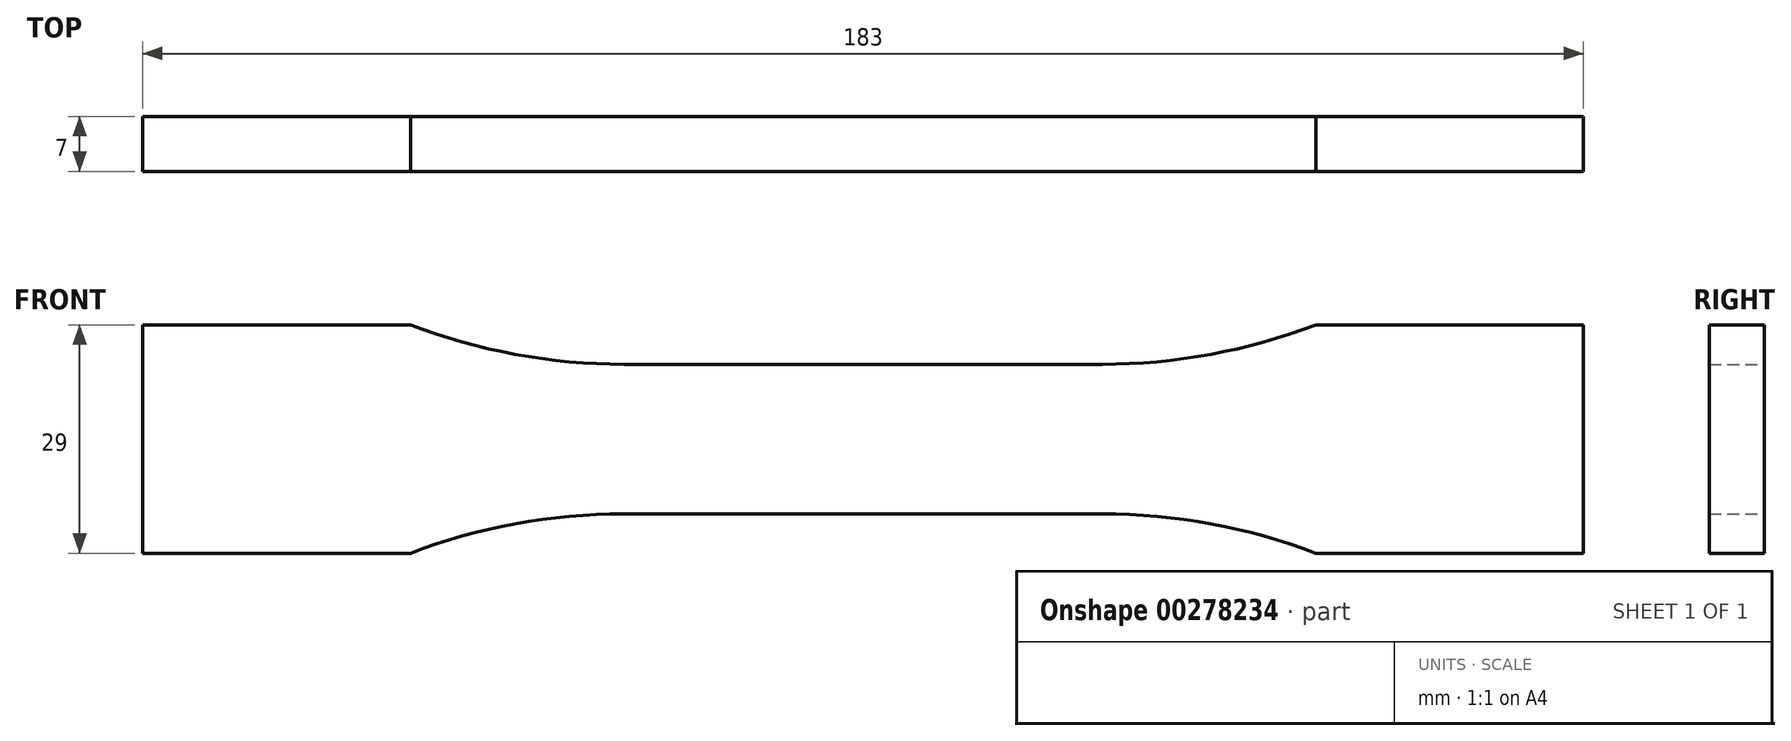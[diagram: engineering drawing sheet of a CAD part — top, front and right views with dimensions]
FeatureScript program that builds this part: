
annotation { "Feature Type Name" : "Feature", "Feature Type Description" : "" }
export const myFeature = defineFeature(function(context is Context, id is Id, definition is map)
    precondition{}
    {
        {
            var Q0;
            Q0=qCreatedBy(makeId("Front.planeOp"),FACE);
            var sketch = newSketch(context, id + "F0", { "sketchPlane" : qUnion([Q0])});
            skLineSegment(sketch, "E0", {"start": v(0, 9.5) * mm, "end": v(30.39, 9.5) * mm});
            skArc(sketch, "E1", {"start": v(30.39, 9.5) * mm, "mid": v(44.17, 10.76) * mm, "end": v(57.5, 14.5) * mm});
            skLineSegment(sketch, "E2", {"start": v(57.5, 14.5) * mm, "end": v(91.5, 14.5) * mm});
            skLineSegment(sketch, "E3.MirrorCS", {"start": v(0, -9.5) * mm, "end": v(30.39, -9.5) * mm});
            skLineSegment(sketch, "E4.MirrorCS", {"start": v(57.5, -14.5) * mm, "end": v(91.5, -14.5) * mm});
            skArc(sketch, "E5.MirrorCS", {"start": v(30.39, -9.5) * mm, "mid": v(44.17, -10.76) * mm, "end": v(57.5, -14.5) * mm});
            skLineSegment(sketch, "E6.MirrorCS", {"start": v(0, 9.5) * mm, "end": v(-30.39, 9.5) * mm});
            skArc(sketch, "E7.MirrorCS", {"start": v(-30.39, 9.5) * mm, "mid": v(-44.17, 10.76) * mm, "end": v(-57.5, 14.5) * mm});
            skLineSegment(sketch, "E8.MirrorCS", {"start": v(-57.5, 14.5) * mm, "end": v(-91.5, 14.5) * mm});
            skArc(sketch, "E9.MirrorCS", {"start": v(-30.39, -9.5) * mm, "mid": v(-44.17, -10.76) * mm, "end": v(-57.5, -14.5) * mm});
            skLineSegment(sketch, "E10.MirrorCS", {"start": v(-57.5, -14.5) * mm, "end": v(-91.5, -14.5) * mm});
            skLineSegment(sketch, "E11.MirrorCS", {"start": v(0, -9.5) * mm, "end": v(-30.39, -9.5) * mm});
            skLineSegment(sketch, "E12", {"start": v(-91.5, 14.5) * mm, "end": v(-91.5, -14.5) * mm});
            skLineSegment(sketch, "E13", {"start": v(91.5, 14.5) * mm, "end": v(91.5, -14.5) * mm});
            skSolve(sketch);
        }
        {
            var Q0;
            Q0 = qSketchRegion(id + "F0", true);
            extrude(context, id + "F1", {"entities" : qUnion([Q0]), "endBound" : BoundingType.SYMMETRIC, "depth" : 7 * mm});
        }
    });
